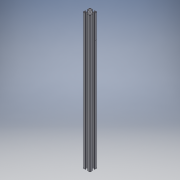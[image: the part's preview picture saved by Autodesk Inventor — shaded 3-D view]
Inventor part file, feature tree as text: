
AUTODESK INVENTOR PART (.ipt)
format: ipt  version: 2019 (Build 230136000, 136)  size: 342,016 bytes
history: native  units: in
note: dims shown in document units (in); Inventor stores cm internally (conversion verified against a paired STEP export)
features: extrude x1, sketch x1, projected_geometry x1
ambient origin geometry x8: Origin, YZ Plane, XZ Plane, XY Plane, X Axis, Y Axis, Z Axis, Center Point
bodies: Solid1 (feature_tree), Body1 (feature_tree)
feature tree (3):
  extrude  "Extrusion1"  [1 undecoded]
  sketch  "Sketch1"  dims[d0=18.5039in d1=0.0in]
  projected_geometry  "Projected Loop1"
note: 1 required parameter value undecoded (feature->parameter linkage not recoverable at this tier; creation-order binding heuristic only, values carry confidence <= 0.55)
